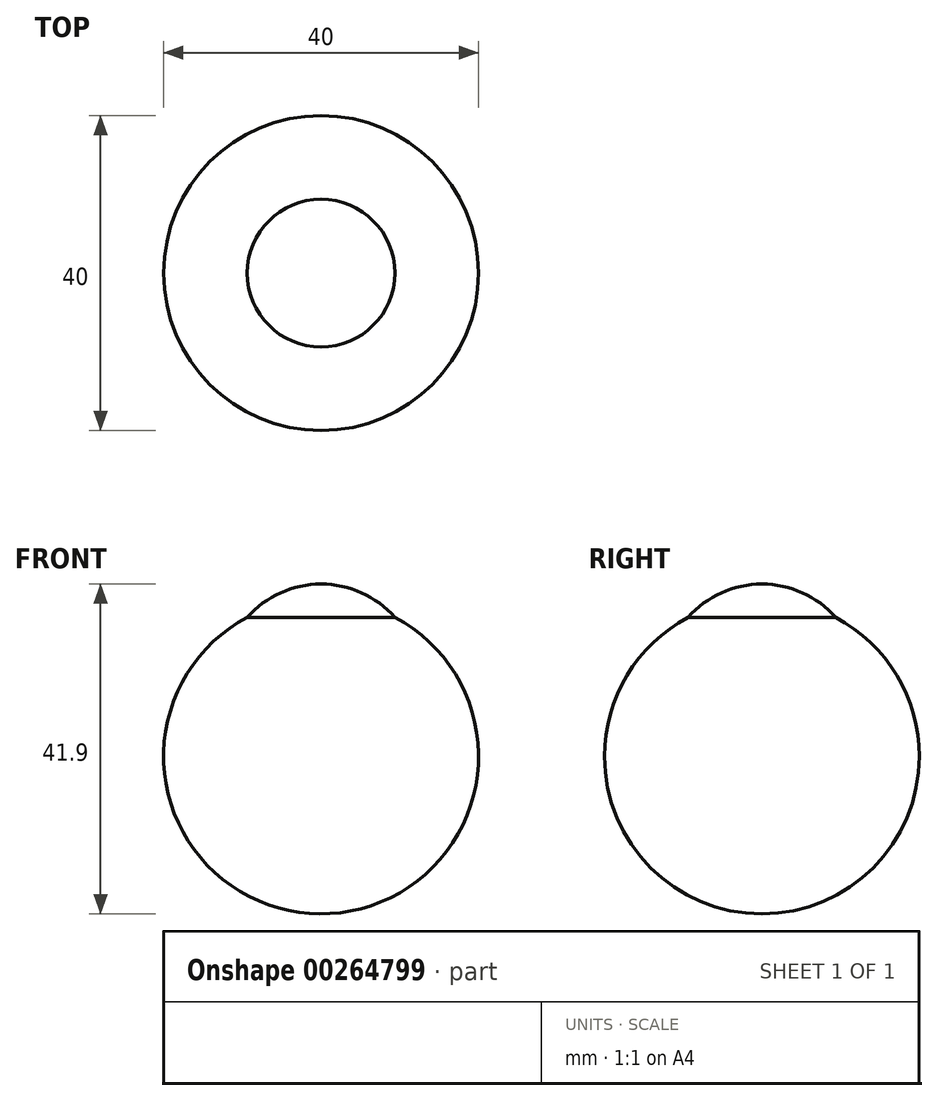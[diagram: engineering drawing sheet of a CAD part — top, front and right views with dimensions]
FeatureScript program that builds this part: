
annotation { "Feature Type Name" : "Feature", "Feature Type Description" : "" }
export const myFeature = defineFeature(function(context is Context, id is Id, definition is map)
    precondition{}
    {
        {
            var Q0;
            Q0=qCreatedBy(makeId("Top.planeOp"),FACE);
            var sketch = newSketch(context, id + "F0", { "sketchPlane" : qUnion([Q0])});
            skCircle(sketch, "E0", {"center": v(0, 0) * mm, "radius": 20 * mm});
            skLineSegment(sketch, "E1", {"start": v(0, 20) * mm, "end": v(0, -20) * mm});
            skSolve(sketch);
        }
        {
            var Q0;
            {var subQ0=sQuery(id+"F0.wireOp",EDGE,"E1");Q0=makeQuery(id+"F0.imprint","IMPRINT",FACE,{"disambiguationData":[TD([[makeQuery(id+"F0.imprint","IMPRINT",EDGE,{"derivedFrom":subQ0}),-1.0]])]});}
            var Q1;
            Q1=sQuery(id+"F0.wireOp",EDGE,"E1");
            revolve(context, id + "F1", {"entities" : qUnion([Q0]), "axis" : qUnion([Q1]), "revolveType" : RevolveType.FULL});
        }
        {
            var Q0;
            Q0=qCreatedBy(makeId("Top.planeOp"),FACE);
            cPlane(context, id + "F2", {"entities" : qUnion([Q0]), "cplaneType" : CPlaneType.OFFSET, "offset" : 9.4 * mm, "width" : 150 * mm, "height" : 150 * mm});
        }
        {
            var Q0;
            Q0=qCreatedBy(id+"F2.planeOp",FACE);
            var sketch = newSketch(context, id + "F3", { "sketchPlane" : qUnion([Q0])});
            skCircle(sketch, "E2", {"center": v(0, 0) * mm, "radius": 12.5 * mm});
            skLineSegment(sketch, "E3", {"start": v(0, 12.5) * mm, "end": v(0, -12.5) * mm});
            skSolve(sketch);
        }
        {
            var Q0;
            {var subQ0=sQuery(id+"F3.wireOp",EDGE,"E3");Q0=makeQuery(id+"F3.imprint","IMPRINT",FACE,{"disambiguationData":[TD([[makeQuery(id+"F3.imprint","IMPRINT",EDGE,{"derivedFrom":subQ0}),-1.0]])]});}
            var Q1;
            Q1=sQuery(id+"F3.wireOp",EDGE,"E3");
            revolve(context, id + "F4", {"operationType" : NewBodyOperationType.ADD, "entities" : qUnion([Q0]), "axis" : qUnion([Q1]), "revolveType" : RevolveType.FULL});
        }
    });
